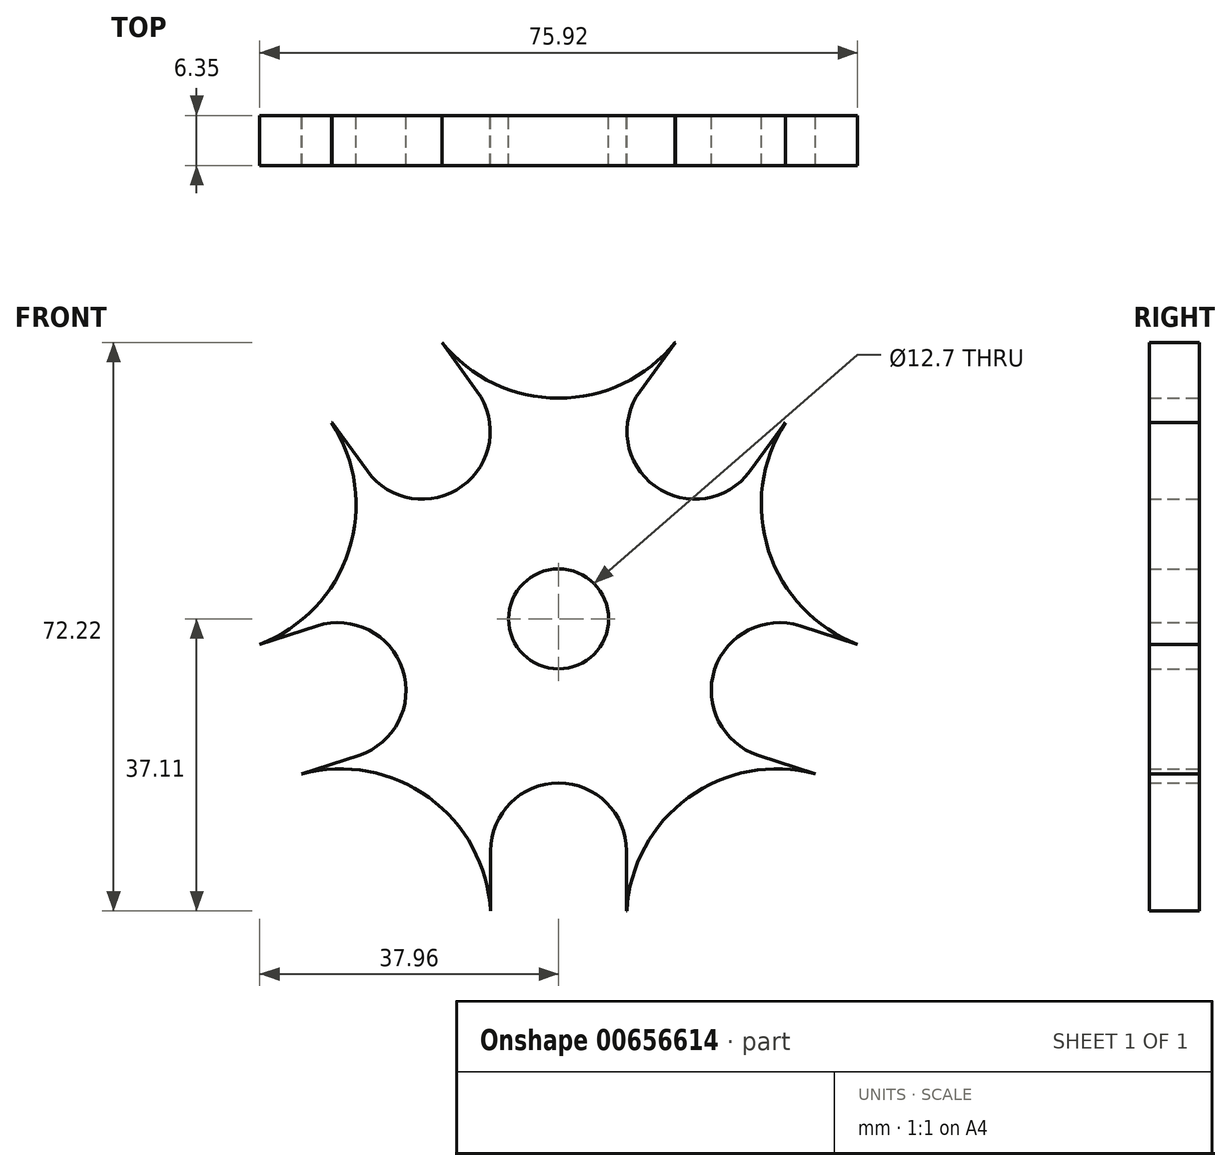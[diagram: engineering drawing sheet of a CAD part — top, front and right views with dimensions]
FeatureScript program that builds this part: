
annotation { "Feature Type Name" : "Feature", "Feature Type Description" : "" }
export const myFeature = defineFeature(function(context is Context, id is Id, definition is map)
    precondition{}
    {
        {
            var Q0;
            Q0=qCreatedBy(makeId("Front.planeOp"),FACE);
            var sketch = newSketch(context, id + "F0", { "sketchPlane" : qUnion([Q0])});
            skCircle(sketch, "E0.cCircle", {"center": v(0, 0) * mm, "radius": 38.1 * mm, "construction": true});
            skLineSegment(sketch, "E0.0", {"start": v(27.68, -38.1) * mm, "end": v(-27.68, -38.1) * mm});
            skLineSegment(sketch, "E0.1", {"start": v(-27.68, -38.1) * mm, "end": v(-44.79, 14.55) * mm});
            skLineSegment(sketch, "E0.2", {"start": v(-44.79, 14.55) * mm, "end": v(0, 47.1) * mm});
            skLineSegment(sketch, "E0.3", {"start": v(0, 47.1) * mm, "end": v(44.79, 14.55) * mm});
            skLineSegment(sketch, "E0.4", {"start": v(44.79, 14.55) * mm, "end": v(27.68, -38.1) * mm});
            skPoint(sketch, "E0.0.midPoint", {"position": v(0, -38.1) * mm});
            skCircle(sketch, "E1", {"center": v(-44.79, 14.55) * mm, "radius": 19.05 * mm});
            skCircle(sketch, "E2", {"center": v(-27.68, -38.1) * mm, "radius": 19.05 * mm});
            skCircle(sketch, "E3", {"center": v(27.68, -38.1) * mm, "radius": 19.05 * mm});
            skCircle(sketch, "E4", {"center": v(44.79, 14.55) * mm, "radius": 19.05 * mm});
            skCircle(sketch, "E5", {"center": v(0, 47.1) * mm, "radius": 19.05 * mm});
            skCircle(sketch, "E6", {"center": v(-22.4, 30.82) * mm, "radius": 8.63 * mm});
            skCircle(sketch, "E7", {"center": v(-36.24, -11.77) * mm, "radius": 8.63 * mm});
            skCircle(sketch, "E8", {"center": v(0, -38.1) * mm, "radius": 8.63 * mm});
            skCircle(sketch, "E9", {"center": v(36.24, -11.77) * mm, "radius": 8.63 * mm});
            skCircle(sketch, "E10", {"center": v(22.4, 30.82) * mm, "radius": 8.63 * mm});
            skCircle(sketch, "E11", {"center": v(0, 0) * mm, "radius": 6.35 * mm});
            skCircle(sketch, "E12", {"center": v(-17.32, 23.84) * mm, "radius": 8.63 * mm});
            skLineSegment(sketch, "E13", {"start": v(-17.32, 23.84) * mm, "end": v(-22.4, 30.82) * mm});
            skLineSegment(sketch, "E14", {"start": v(-15.41, 35.9) * mm, "end": v(-10.34, 28.91) * mm});
            skLineSegment(sketch, "E15", {"start": v(-24.3, 18.77) * mm, "end": v(-29.38, 25.75) * mm});
            skCircle(sketch, "E16.1.0", {"center": v(-28.03, -9.1) * mm, "radius": 8.63 * mm});
            skLineSegment(sketch, "E16.1.1", {"start": v(-25.36, -17.32) * mm, "end": v(-33.57, -19.98) * mm});
            skLineSegment(sketch, "E16.1.2", {"start": v(-28.03, -9.1) * mm, "end": v(-36.24, -11.77) * mm});
            skLineSegment(sketch, "E16.1.3", {"start": v(-38.9, -3.56) * mm, "end": v(-30.7, -0.9) * mm});
            skCircle(sketch, "E16.2.0", {"center": v(0, -29.47) * mm, "radius": 8.63 * mm});
            skLineSegment(sketch, "E16.2.1", {"start": v(8.63, -29.47) * mm, "end": v(8.63, -38.1) * mm});
            skLineSegment(sketch, "E16.2.2", {"start": v(0, -29.47) * mm, "end": v(0, -38.1) * mm});
            skLineSegment(sketch, "E16.2.3", {"start": v(-8.63, -38.1) * mm, "end": v(-8.63, -29.47) * mm});
            skCircle(sketch, "E16.3.0", {"center": v(28.03, -9.1) * mm, "radius": 8.63 * mm});
            skLineSegment(sketch, "E16.3.1", {"start": v(30.7, -0.9) * mm, "end": v(38.9, -3.56) * mm});
            skLineSegment(sketch, "E16.3.2", {"start": v(28.03, -9.1) * mm, "end": v(36.24, -11.77) * mm});
            skLineSegment(sketch, "E16.3.3", {"start": v(33.57, -19.98) * mm, "end": v(25.36, -17.32) * mm});
            skCircle(sketch, "E16.4.0", {"center": v(17.32, 23.84) * mm, "radius": 8.63 * mm});
            skLineSegment(sketch, "E16.4.1", {"start": v(10.34, 28.91) * mm, "end": v(15.41, 35.9) * mm});
            skLineSegment(sketch, "E16.4.2", {"start": v(17.32, 23.84) * mm, "end": v(22.4, 30.82) * mm});
            skLineSegment(sketch, "E16.4.3", {"start": v(29.38, 25.75) * mm, "end": v(24.3, 18.77) * mm});
            skCircle(sketch, "E17", {"center": v(0, 0) * mm, "radius": 38.1 * mm});
            skSolve(sketch);
        }
        {
            var Q0;
            Q0=makeQuery(id+"F0.imprint","IMPRINT",FACE,{"disambiguationData":[TD([[makeQuery(id+"F0.imprint","IMPRINT",EDGE,{"derivedFrom":sQuery(id+"F0.wireOp",EDGE,"E11")}),-1.0]])]});
            extrude(context, id + "F1", {"entities" : qUnion([Q0]), "depth" : 6.35 * mm, "offsetDistance" : 25.4 * mm});
        }
    });
